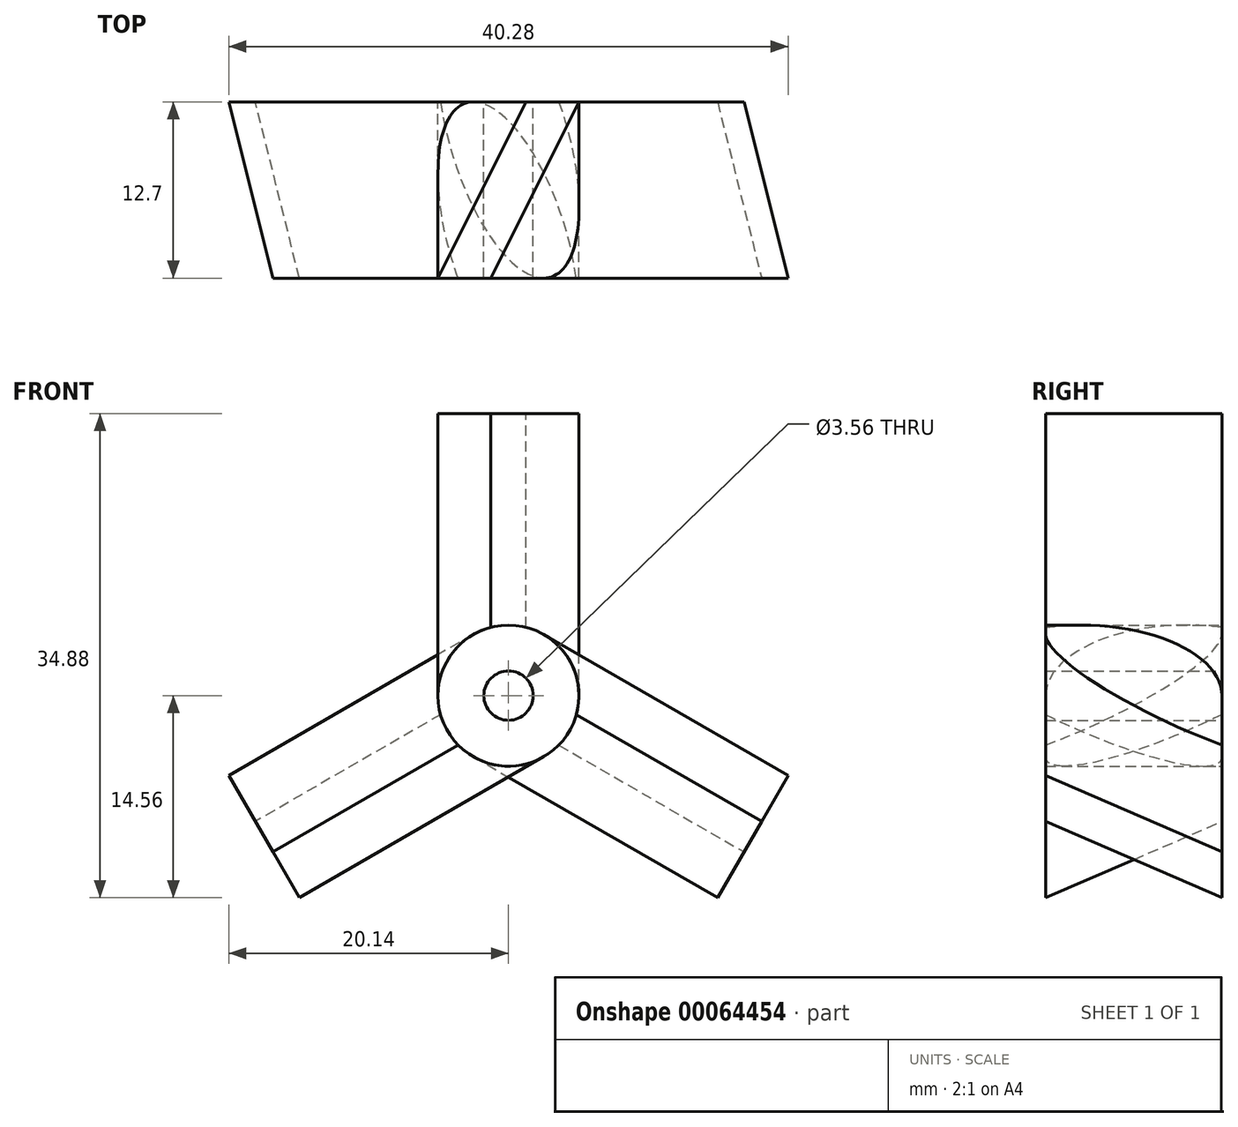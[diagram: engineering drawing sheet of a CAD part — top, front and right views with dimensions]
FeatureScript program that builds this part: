
annotation { "Feature Type Name" : "Feature", "Feature Type Description" : "" }
export const myFeature = defineFeature(function(context is Context, id is Id, definition is map)
    precondition{}
    {
        {
            var Q0;
            Q0=qCreatedBy(makeId("Front.planeOp"),FACE);
            var sketch = newSketch(context, id + "F0", { "sketchPlane" : qUnion([Q0])});
            skCircle(sketch, "E0", {"center": v(0, 0) * mm, "radius": 5.08 * mm});
            skCircle(sketch, "E1", {"center": v(0, 0) * mm, "radius": 1.78 * mm});
            skPoint(sketch, "E2", {"position": v(-4.4, 2.54) * mm});
            skPoint(sketch, "E3", {"position": v(4.4, 2.54) * mm});
            skPoint(sketch, "E4", {"position": v(0, -5.08) * mm});
            skLineSegment(sketch, "E5", {"start": v(-4.4, 2.54) * mm, "end": v(0, 0) * mm, "construction": true});
            skLineSegment(sketch, "E6", {"start": v(0, 0) * mm, "end": v(4.4, 2.54) * mm, "construction": true});
            skLineSegment(sketch, "E7", {"start": v(0, 0) * mm, "end": v(0, -5.08) * mm, "construction": true});
            skSolve(sketch);
        }
        {
            var Q0;
            Q0 = qSketchRegion(id + "F0", true);
            extrude(context, id + "F1", {"entities" : qUnion([Q0]), "depth" : 12.7 * mm});
        }
        {
            var Q0;
            Q0=qCreatedBy(makeId("Top.planeOp"),FACE);
            cPlane(context, id + "F2", {"entities" : qUnion([Q0]), "cplaneType" : CPlaneType.OFFSET, "offset" : 20.32 * mm, "width" : 152.4 * mm, "height" : 152.4 * mm});
        }
        {
            var Q0;
            Q0=qCreatedBy(id+"F2.planeOp",FACE);
            var sketch = newSketch(context, id + "F3", { "sketchPlane" : qUnion([Q0])});
            skLineSegment(sketch, "E8", {"start": v(5.08, 0) * mm, "end": v(-1.27, -12.7) * mm});
            skLineSegment(sketch, "E9", {"start": v(-1.27, -12.7) * mm, "end": v(-5.08, -12.7) * mm});
            skLineSegment(sketch, "E10", {"start": v(-5.08, -12.7) * mm, "end": v(1.27, 0) * mm});
            skLineSegment(sketch, "E11", {"start": v(1.27, 0) * mm, "end": v(5.08, 0) * mm});
            skLineSegment(sketch, "E12", {"start": v(0, -21.45) * mm, "end": v(0, 7.18) * mm, "construction": true});
            skSolve(sketch);
        }
        {
            var Q0;
            Q0 = qSketchRegion(id + "F3", true);
            extrude(context, id + "F4", {"entities" : qUnion([Q0]), "endBound" : BoundingType.UP_TO_NEXT, "oppositeDirection" : true, "depth" : 25.4 * mm});
        }
        {
            var Q0;
            Q0=qCreatedBy(makeId("Top.planeOp"),FACE);
            var sketch = newSketch(context, id + "F5", { "sketchPlane" : qUnion([Q0])});
            skLineSegment(sketch, "E13", {"start": v(0, -28.14) * mm, "end": v(0, 28.84) * mm, "construction": true});
            skSolve(sketch);
        }
        {
            var Q0;
            Q0=makeQuery(id+"F4.opExtrude","SWEPT_BODY",BODY,{"disambiguationData":[OSD([sQuery(id+"F3.wireOp",EDGE,"E8"),sQuery(id+"F3.wireOp",EDGE,"E9"),sQuery(id+"F3.wireOp",EDGE,"E10"),sQuery(id+"F3.wireOp",EDGE,"E11")])]});
            var Q1;
            Q1=sQuery(id+"F5.wireOp",EDGE,"E13");
            circularPattern(context, id + "F6", {"entities" : qUnion([Q0]), "axis" : qUnion([Q1]), "angle" : 120 * degree, "instanceCount" : 3});
        }
    });
